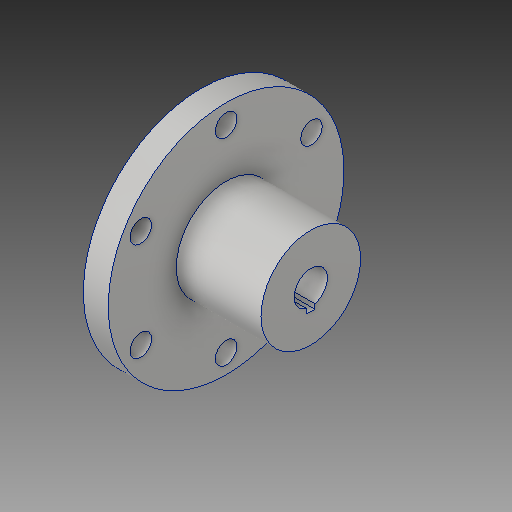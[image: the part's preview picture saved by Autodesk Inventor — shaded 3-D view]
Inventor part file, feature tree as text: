
AUTODESK INVENTOR PART (.ipt)
format: ipt  version: 2019 (Build 230136000, 136)  size: 150,528 bytes
history: native  units: mm
features: sketch x5, extrude x3, hole x2, other x1
ambient origin geometry x8: Origin, YZ Plane, XZ Plane, XY Plane, X Axis, Y Axis, Z Axis, Center Point
bodies: Body1 (feature_tree)
feature tree (11):
  other  "ソリッド1"
  sketch  "スケッチ1"
  extrude  "押し出し1"  Depth=56.8mm
  extrude  "押し出し2"  Depth=6.0mm TaperAngle=0.0deg
  hole  "穴2"  [1 undecoded]
  extrude  "押し出し5"  Depth=20.4mm TaperAngle=0.0deg
  hole  "穴3"  [1 undecoded]
  sketch  "スケッチ2"
  sketch  "スケッチ3"
  sketch  "スケッチ6"
  sketch  "スケッチ7"
note: 2 required parameter values undecoded (feature->parameter linkage not recoverable at this tier; creation-order binding heuristic only, values carry confidence <= 0.55)
